# Revit family: Hager-Golf-IP40-Plain_Door-syst-NoHosted-PL-pl
name_source: partatom
category: Electrical Equipment
units: mm (PartAtom-declared; Revit-internal decimal feet)

## family parameters
Always vertical = Yes
Cut with Voids When Loaded = No
Panel Configuration = Two Columns, Circuits Across
Part Type = Panelboard
Room Calculation Point = No
Round Connector Dimension = Use Diameter
Shared = No
Work Plane-Based = Yes

## types (36) — shared parameters
Default Elevation = 1219 mm
EF000116 - Numer RAL = 9010
EF001062 - Wykonane zgodnie z Dyrektywą Kompatybilności Elektromagnetycznej EMC = No
EF004462 - Rodzaj zamknięcia = EV000154 - Inne
EF006244 - Transparentna pokrywa/drzwi = No
EF006306 - Z zamkiem = No
HG000001 - Liczba kolumn = 1
HG000002 - Z drzwiami lub pokrywą = Yes
HG000003 - Zakres = Golf
HG000005 - Grubość = 3 mm  [stored 0.00984252 ft]
HG000009 - Drzwi dwuskrzydłowe = No
HG000010 - Drzwi asymetryczne = No
HG000011 - Puste rzędy od dołu = No
HG000017 - Odległość między biegunami = 18 mm  [stored 0.0590551 ft]
Manufacturer = Hager
Type Comments = Golf
zero-valued in all types: HG000007 - Liczba pustych kolumn, HG000008 - Liczba pustych rzędów

## per-type parameters (varying)
| type | EF000003 - Sposób montażu | EF000007 - Kolor | EF000008 - Szerokość | EF000040 - Wysokość | EF000049 - Głębokość | EF000118 - Z płytą montażową | EF000218 - Głębokość wbudowania | EF000266 - Liczba rzędów | EF000332 - Wysokość wbudowania | EF000339 - Rodzaj pokrywy | EF000846 - Szerokość wbudowania | EF001088 - Możliwość rozbudowy | EF001131 - Głębokość wewnętrzna | EF001134 - Szyna DIN | EF001596 - Materiał obudowy | EF002950 - Szerokość wyrażona liczbą modułów | EF005474 - Stopień ochrony (IP) | EF009212 - Wykonanie pokrywy | EF015776 - Listwa zaciskowa uziemienia | EF015777 - Listwa zaciskowa przewodu neutralnego | EF015941 - Drzwi przepuszczające sygnał | HG000004 - Referencja producenta | HG000006 - Montaż podtynkowy | Model |
| Montaż natynkowy  S137.5 W183.5 G98.5 4 Jednostki dywizyjne - VS104PD | EV000384 - Montaż natynkowy |  | 138 mm  [stored 0.452756 ft] | 184 mm  [stored 0.603675 ft] | 98 mm  [stored 0.321522 ft] | No | 0 mm  [stored 0 ft] | 1 | 0 mm  [stored 0 ft] |  | 0 mm  [stored 0 ft] | No | 0 mm  [stored 0 ft] | No |  | 4 |  |  | No | No | No | VS104PD | No | VS104PD |
| Montaż natynkowy  S282 W252 G99 12 Jednostki dywizyjne - VS112PZB | EV000384 - Montaż natynkowy | EV000202 - Biały | 282 mm | 252 mm  [stored 0.826772 ft] | 99 mm  [stored 0.324803 ft] | No | 0 mm  [stored 0 ft] | 1 | 0 mm  [stored 0 ft] | EV004216 - Drzwi | 0 mm  [stored 0 ft] | Yes | 99 mm  [stored 0.324803 ft] | Yes | EV000139 - Tworzywo sztuczne | 12 |  | EV009916 - Z otworem | No | No | Yes | VS112PZB | No | VS112PZB |
| Montaż natynkowy  S282 W377 G99 12 Jednostki dywizyjne - VS212PZB | EV000384 - Montaż natynkowy | EV000202 - Biały | 282 mm | 377 mm  [stored 1.23688 ft] | 99 mm  [stored 0.324803 ft] | No | 0 mm  [stored 0 ft] | 2 | 0 mm  [stored 0 ft] | EV004216 - Drzwi | 0 mm  [stored 0 ft] | Yes | 99 mm  [stored 0.324803 ft] | Yes | EV000139 - Tworzywo sztuczne | 12 |  | EV009916 - Z otworem | No | No | Yes | VS212PZB | No | VS212PZB |
| Montaż natynkowy  S390 W377 G99 18 Jednostki dywizyjne - VS218PZE | EV000384 - Montaż natynkowy | EV000202 - Biały | 390 mm  [stored 1.27953 ft] | 377 mm  [stored 1.23688 ft] | 99 mm  [stored 0.324803 ft] | Yes | 0 mm  [stored 0 ft] | 2 | 0 mm  [stored 0 ft] | EV004216 - Drzwi | 0 mm  [stored 0 ft] | Yes | 99 mm  [stored 0.324803 ft] | Yes | EV000139 - Tworzywo sztuczne | 18 |  | EV009916 - Z otworem | No | No | Yes | VS218PZE | No | VS218PZE |
| Montaż natynkowy  S390 W377 G99 18 Jednostki dywizyjne - VS218PZF | EV000384 - Montaż natynkowy | EV000202 - Biały | 390 mm  [stored 1.27953 ft] | 377 mm  [stored 1.23688 ft] | 99 mm  [stored 0.324803 ft] | Yes | 0 mm  [stored 0 ft] | 2 | 0 mm  [stored 0 ft] | EV004216 - Drzwi | 0 mm  [stored 0 ft] | Yes | 99 mm  [stored 0.324803 ft] | Yes | EV000139 - Tworzywo sztuczne | 18 |  | EV009916 - Z otworem | No | No | Yes | VS218PZF | No | VS218PZF |
| Montaż natynkowy  S390 W500 G99 18 Jednostki dywizyjne - VS318PZF | EV000384 - Montaż natynkowy | EV000202 - Biały | 390 mm  [stored 1.27953 ft] | 500 mm  [stored 1.64042 ft] | 99 mm  [stored 0.324803 ft] | Yes | 0 mm  [stored 0 ft] | 3 | 0 mm  [stored 0 ft] | EV004216 - Drzwi | 0 mm  [stored 0 ft] | Yes | 99 mm  [stored 0.324803 ft] | Yes | EV000139 - Tworzywo sztuczne | 18 |  | EV009916 - Z otworem | No | No | Yes | VS318PZF | No | VS318PZF |
| Montaż natynkowy  S390 W647 G99 18 Jednostki dywizyjne - VS418PZF | EV000384 - Montaż natynkowy | EV000202 - Biały | 390 mm  [stored 1.27953 ft] | 647 mm  [stored 2.1227 ft] | 99 mm  [stored 0.324803 ft] | Yes | 0 mm  [stored 0 ft] | 4 | 0 mm  [stored 0 ft] | EV004216 - Drzwi | 0 mm  [stored 0 ft] | Yes | 99 mm  [stored 0.324803 ft] | Yes | EV000139 - Tworzywo sztuczne | 18 |  | EV009916 - Z otworem | No | No | Yes | VS418PZF | No | VS418PZF |
| Montaż natynkowy IP40 S209.5 W183.5 G98.5 8 Jednostki dywizyjne - VS108PD | EV000384 - Montaż natynkowy |  | 210 mm  [stored 0.688976 ft] | 184 mm  [stored 0.603675 ft] | 98 mm  [stored 0.321522 ft] | No | 0 mm  [stored 0 ft] | 1 | 0 mm  [stored 0 ft] |  | 0 mm  [stored 0 ft] | No | 0 mm  [stored 0 ft] | No |  | 8 | EV006415 - IP40 |  | No | No | No | VS108PD | No | VS108PD |
| Montaż natynkowy IP40 S281.5 W251.5 G98.5 12 Jednostki dywizyjne - VS112PD | EV000384 - Montaż natynkowy |  | 282 mm | 252 mm  [stored 0.826772 ft] | 98 mm  [stored 0.321522 ft] | No | 0 mm  [stored 0 ft] | 1 | 0 mm  [stored 0 ft] |  | 0 mm  [stored 0 ft] | No | 0 mm  [stored 0 ft] | No |  | 12 | EV006415 - IP40 |  | No | No | No | VS112PD | No | VS112PD |
| Montaż natynkowy IP40 S282 W377 G99 12 Jednostki dywizyjne - VS212PD | EV000384 - Montaż natynkowy | EV000202 - Biały | 282 mm | 377 mm  [stored 1.23688 ft] | 99 mm  [stored 0.324803 ft] | No | 0 mm  [stored 0 ft] | 2 | 0 mm  [stored 0 ft] | EV004216 - Drzwi | 0 mm  [stored 0 ft] | Yes | 99 mm  [stored 0.324803 ft] | Yes | EV000139 - Tworzywo sztuczne | 12 | EV006415 - IP40 | EV000116 - Zamknięty | Yes | Yes | Yes | VS212PD | No | VS212PD |
| Montaż natynkowy IP40 S282 W500 G99 12 Jednostki dywizyjne - VS312PD | EV000384 - Montaż natynkowy | EV000202 - Biały | 282 mm | 500 mm  [stored 1.64042 ft] | 99 mm  [stored 0.324803 ft] | No | 0 mm  [stored 0 ft] | 3 | 0 mm  [stored 0 ft] | EV004216 - Drzwi | 0 mm  [stored 0 ft] | Yes | 99 mm  [stored 0.324803 ft] | Yes | EV000139 - Tworzywo sztuczne | 12 | EV006415 - IP40 | EV000116 - Zamknięty | Yes | Yes | Yes | VS312PD | No | VS312PD |
| Montaż natynkowy IP40 S282 W647 G99 12 Jednostki dywizyjne - VS412PD | EV000384 - Montaż natynkowy | EV000202 - Biały | 282 mm | 647 mm  [stored 2.1227 ft] | 99 mm  [stored 0.324803 ft] | No | 0 mm  [stored 0 ft] | 4 | 0 mm  [stored 0 ft] | EV004216 - Drzwi | 0 mm  [stored 0 ft] | Yes | 99 mm  [stored 0.324803 ft] | Yes | EV000139 - Tworzywo sztuczne | 12 | EV006415 - IP40 | EV000116 - Zamknięty | Yes | Yes | Yes | VS412PD | No | VS412PD |
| Montaż natynkowy IP40 S390 W252 G99 18 Jednostki dywizyjne - VS118PD | EV000384 - Montaż natynkowy | EV000202 - Biały | 390 mm  [stored 1.27953 ft] | 252 mm  [stored 0.826772 ft] | 99 mm  [stored 0.324803 ft] | No | 0 mm  [stored 0 ft] | 1 | 0 mm  [stored 0 ft] | EV004216 - Drzwi | 0 mm  [stored 0 ft] | Yes | 99 mm  [stored 0.324803 ft] | Yes | EV000139 - Tworzywo sztuczne | 18 | EV006415 - IP40 | EV000116 - Zamknięty | Yes | Yes | Yes | VS118PD | No | VS118PD |
| Montaż natynkowy IP40 S390 W377 G99 18 Jednostki dywizyjne - VS218PD | EV000384 - Montaż natynkowy | EV000202 - Biały | 390 mm  [stored 1.27953 ft] | 377 mm  [stored 1.23688 ft] | 99 mm  [stored 0.324803 ft] | No | 0 mm  [stored 0 ft] | 2 | 0 mm  [stored 0 ft] | EV004216 - Drzwi | 0 mm  [stored 0 ft] | Yes | 99 mm  [stored 0.324803 ft] | Yes | EV000139 - Tworzywo sztuczne | 18 | EV006415 - IP40 | EV000116 - Zamknięty | Yes | Yes | Yes | VS218PD | No | VS218PD |
| Montaż natynkowy IP40 S390 W377 G99 18 Jednostki dywizyjne - VS218PDE | EV000384 - Montaż natynkowy | EV000202 - Biały | 390 mm  [stored 1.27953 ft] | 377 mm  [stored 1.23688 ft] | 99 mm  [stored 0.324803 ft] | No | 0 mm  [stored 0 ft] | 2 | 0 mm  [stored 0 ft] | EV004216 - Drzwi | 0 mm  [stored 0 ft] | Yes | 99 mm  [stored 0.324803 ft] | Yes | EV000139 - Tworzywo sztuczne | 18 | EV006415 - IP40 | EV000116 - Zamknięty | Yes | Yes | Yes | VS218PDE | No | VS218PDE |
| Montaż natynkowy IP40 S390 W500 G99 18 Jednostki dywizyjne - VS318PD | EV000384 - Montaż natynkowy | EV000202 - Biały | 390 mm  [stored 1.27953 ft] | 500 mm  [stored 1.64042 ft] | 99 mm  [stored 0.324803 ft] | No | 0 mm  [stored 0 ft] | 3 | 0 mm  [stored 0 ft] | EV004216 - Drzwi | 0 mm  [stored 0 ft] | Yes | 99 mm  [stored 0.324803 ft] | Yes | EV000139 - Tworzywo sztuczne | 18 | EV006415 - IP40 | EV000116 - Zamknięty | Yes | Yes | Yes | VS318PD | No | VS318PD |
| Montaż natynkowy IP40 S390 W647 G99 18 Jednostki dywizyjne - VS418PD | EV000384 - Montaż natynkowy | EV000202 - Biały | 390 mm  [stored 1.27953 ft] | 647 mm  [stored 2.1227 ft] | 99 mm  [stored 0.324803 ft] | No | 0 mm  [stored 0 ft] | 4 | 0 mm  [stored 0 ft] | EV004216 - Drzwi | 0 mm  [stored 0 ft] | Yes | 99 mm  [stored 0.324803 ft] | Yes | EV000139 - Tworzywo sztuczne | 18 | EV006415 - IP40 | EV000116 - Zamknięty | Yes | Yes | Yes | VS418PD | No | VS418PD |
| Montaż natynkowy IP40 S462 W252 G99 22 Jednostki dywizyjne - VS122PD | EV000384 - Montaż natynkowy | EV000202 - Biały | 462 mm  [stored 1.51575 ft] | 252 mm  [stored 0.826772 ft] | 99 mm  [stored 0.324803 ft] | No | 0 mm  [stored 0 ft] | 1 | 0 mm  [stored 0 ft] | EV004216 - Drzwi | 0 mm  [stored 0 ft] | Yes | 99 mm  [stored 0.324803 ft] | Yes | EV000139 - Tworzywo sztuczne | 22 | EV006415 - IP40 | EV000116 - Zamknięty | Yes | Yes | Yes | VS122PD | No | VS122PD |
| Montaż podtynkowy  S204 W225 G97.5 4 Jednostki dywizyjne - VF104PD | EV000383 - Montaż podtynkowy |  | 204 mm | 225 mm  [stored 0.738189 ft] | 98 mm  [stored 0.321522 ft] | No | 72 mm  [stored 0.23622 ft] | 1 | 189 mm  [stored 0.620079 ft] |  | 170 mm  [stored 0.557743 ft] | No | 0 mm  [stored 0 ft] | No | EV000139 - Tworzywo sztuczne | 4 |  |  | No | No | No | VF104PD | Yes | VF104PD |
| Montaż podtynkowy  S275 W225 G97.5 8 Jednostki dywizyjne - VF108PD | EV000383 - Montaż podtynkowy |  | 275 mm | 225 mm  [stored 0.738189 ft] | 98 mm  [stored 0.321522 ft] | No | 72 mm  [stored 0.23622 ft] | 1 | 189 mm  [stored 0.620079 ft] |  | 242 mm  [stored 0.793963 ft] | No | 0 mm  [stored 0 ft] | No | EV000139 - Tworzywo sztuczne | 8 |  |  | No | No | No | VF108PD | Yes | VF108PD |
| Montaż podtynkowy  S352 W293 G97.5 12 Jednostki dywizyjne - VF112PZB | EV000383 - Montaż podtynkowy | EV000202 - Biały | 352 mm  [stored 1.15486 ft] | 293 mm | 98 mm  [stored 0.321522 ft] | No | 72 mm  [stored 0.23622 ft] | 1 | 250 mm  [stored 0.82021 ft] | EV004216 - Drzwi | 318 mm  [stored 1.04331 ft] | Yes | 98 mm  [stored 0.321522 ft] | Yes | EV000139 - Tworzywo sztuczne | 12 |  | EV009916 - Z otworem | No | No | Yes | VF112PZB | Yes | VF112PZB |
| Montaż podtynkowy  S352 W543 G97.5 12 Jednostki dywizyjne - VF312PZB | EV000383 - Montaż podtynkowy | EV000202 - Biały | 352 mm  [stored 1.15486 ft] | 543 mm  [stored 1.7815 ft] | 98 mm  [stored 0.321522 ft] | No | 72 mm  [stored 0.23622 ft] | 3 | 495 mm  [stored 1.62402 ft] | EV004216 - Drzwi | 318 mm  [stored 1.04331 ft] | Yes | 98 mm  [stored 0.321522 ft] | Yes | EV000139 - Tworzywo sztuczne | 12 |  | EV009916 - Z otworem | No | No | Yes | VF312PZB | Yes | VF312PZB |
| Montaż podtynkowy  S382 W418 G97.5 12 Jednostki dywizyjne - VF212PZB | EV000383 - Montaż podtynkowy | EV000202 - Biały | 382 mm  [stored 1.25328 ft] | 418 mm  [stored 1.37139 ft] | 98 mm  [stored 0.321522 ft] | No | 72 mm  [stored 0.23622 ft] | 2 | 370 mm  [stored 1.21391 ft] | EV004216 - Drzwi | 318 mm  [stored 1.04331 ft] | Yes | 98 mm  [stored 0.321522 ft] | Yes | EV000139 - Tworzywo sztuczne | 12 |  | EV009916 - Z otworem | No | No | Yes | VF212PZB | Yes | VF212PZB |
| Montaż podtynkowy  S460 W418 G97.5 18 Jednostki dywizyjne - VF218PZB | EV000383 - Montaż podtynkowy | EV000202 - Biały | 460 mm  [stored 1.50919 ft] | 418 mm  [stored 1.37139 ft] | 98 mm  [stored 0.321522 ft] | No | 72 mm  [stored 0.23622 ft] | 2 | 375 mm  [stored 1.23031 ft] | EV004216 - Drzwi | 426 mm  [stored 1.39764 ft] | Yes | 98 mm  [stored 0.321522 ft] | Yes | EV000139 - Tworzywo sztuczne | 18 |  | EV009916 - Z otworem | No | No | Yes | VF218PZB | Yes | VF218PZB |
| Montaż podtynkowy  S460 W418 G97.5 18 Jednostki dywizyjne - VF218PZF | EV000383 - Montaż podtynkowy | EV000202 - Biały | 460 mm  [stored 1.50919 ft] | 418 mm  [stored 1.37139 ft] | 98 mm  [stored 0.321522 ft] | Yes | 72 mm  [stored 0.23622 ft] | 2 | 375 mm  [stored 1.23031 ft] | EV004216 - Drzwi | 426 mm  [stored 1.39764 ft] | Yes | 98 mm  [stored 0.321522 ft] | Yes | EV000139 - Tworzywo sztuczne | 18 |  | EV009916 - Z otworem | No | No | Yes | VF218PZF | Yes | VF218PZF |
| Montaż podtynkowy  S460 W543 G97.5 18 Jednostki dywizyjne - VF318PZF | EV000383 - Montaż podtynkowy | EV000202 - Biały | 460 mm  [stored 1.50919 ft] | 543 mm  [stored 1.7815 ft] | 98 mm  [stored 0.321522 ft] | Yes | 72 mm  [stored 0.23622 ft] | 3 | 495 mm  [stored 1.62402 ft] | EV004216 - Drzwi | 426 mm  [stored 1.39764 ft] | Yes | 98 mm  [stored 0.321522 ft] | Yes | EV000139 - Tworzywo sztuczne | 18 |  | EV009916 - Z otworem | No | No | Yes | VF318PZF | Yes | VF318PZF |
| Montaż podtynkowy  S460 W688 G97.5 18 Jednostki dywizyjne - VF418PZF | EV000383 - Montaż podtynkowy | EV000202 - Biały | 460 mm  [stored 1.50919 ft] | 688 mm | 98 mm  [stored 0.321522 ft] | Yes | 72 mm  [stored 0.23622 ft] | 4 | 640 mm  [stored 2.09974 ft] | EV004216 - Drzwi | 426 mm  [stored 1.39764 ft] | Yes | 98 mm  [stored 0.321522 ft] | Yes | EV000139 - Tworzywo sztuczne | 18 |  | EV009916 - Z otworem | No | No | Yes | VF418PZF | Yes | VF418PZF |
| Montaż podtynkowy IP40 S352 W293 G97.5 12 Jednostki dywizyjne - VF112PD | EV000383 - Montaż podtynkowy |  | 352 mm  [stored 1.15486 ft] | 293 mm | 98 mm  [stored 0.321522 ft] | No | 72 mm  [stored 0.23622 ft] | 1 | 257 mm  [stored 0.843176 ft] |  | 318 mm  [stored 1.04331 ft] | No | 0 mm  [stored 0 ft] | No | EV000139 - Tworzywo sztuczne | 12 | EV006415 - IP40 |  | No | No | No | VF112PD | Yes | VF112PD |
| Montaż podtynkowy IP40 S352 W543 G97.5 12 Jednostki dywizyjne - VF312PD | EV000383 - Montaż podtynkowy | EV000202 - Biały | 352 mm  [stored 1.15486 ft] | 543 mm  [stored 1.7815 ft] | 98 mm  [stored 0.321522 ft] | No | 72 mm  [stored 0.23622 ft] | 3 | 507 mm  [stored 1.66339 ft] | EV004216 - Drzwi | 318 mm  [stored 1.04331 ft] | Yes | 98 mm  [stored 0.321522 ft] | Yes | EV000139 - Tworzywo sztuczne | 12 | EV006415 - IP40 | EV000116 - Zamknięty | Yes | Yes | Yes | VF312PD | Yes | VF312PD |
| Montaż podtynkowy IP40 S352 W688 G97.5 12 Jednostki dywizyjne - VF412PD | EV000383 - Montaż podtynkowy | EV000202 - Biały | 352 mm  [stored 1.15486 ft] | 688 mm | 98 mm  [stored 0.321522 ft] | No | 72 mm  [stored 0.23622 ft] | 4 | 652 mm  [stored 2.13911 ft] | EV004216 - Drzwi | 318 mm  [stored 1.04331 ft] | Yes | 98 mm  [stored 0.321522 ft] | Yes | EV000139 - Tworzywo sztuczne | 12 | EV006415 - IP40 | EV000116 - Zamknięty | Yes | Yes | Yes | VF412PD | Yes | VF412PD |
| Montaż podtynkowy IP40 S382 W418 G97.5 12 Jednostki dywizyjne - VF212PD | EV000383 - Montaż podtynkowy | EV000202 - Biały | 382 mm  [stored 1.25328 ft] | 418 mm  [stored 1.37139 ft] | 98 mm  [stored 0.321522 ft] | No | 72 mm  [stored 0.23622 ft] | 2 | 382 mm  [stored 1.25328 ft] | EV004216 - Drzwi | 318 mm  [stored 1.04331 ft] | Yes | 98 mm  [stored 0.321522 ft] | Yes | EV000139 - Tworzywo sztuczne | 12 | EV006415 - IP40 | EV000116 - Zamknięty | Yes | Yes | Yes | VF212PD | Yes | VF212PD |
| Montaż podtynkowy IP40 S460 W293 G97.5 18 Jednostki dywizyjne - VF118PD | EV000383 - Montaż podtynkowy | EV000202 - Biały | 460 mm  [stored 1.50919 ft] | 293 mm | 98 mm  [stored 0.321522 ft] | No | 72 mm  [stored 0.23622 ft] | 1 | 257 mm  [stored 0.843176 ft] | EV004216 - Drzwi | 426 mm  [stored 1.39764 ft] | Yes | 98 mm  [stored 0.321522 ft] | Yes | EV000139 - Tworzywo sztuczne | 18 | EV006415 - IP40 | EV000116 - Zamknięty | Yes | Yes | Yes | VF118PD | Yes | VF118PD |
| Montaż podtynkowy IP40 S460 W418 G97.5 18 Jednostki dywizyjne - VF218PD | EV000383 - Montaż podtynkowy | EV000202 - Biały | 460 mm  [stored 1.50919 ft] | 418 mm  [stored 1.37139 ft] | 98 mm  [stored 0.321522 ft] | No | 72 mm  [stored 0.23622 ft] | 2 | 382 mm  [stored 1.25328 ft] | EV004216 - Drzwi | 426 mm  [stored 1.39764 ft] | Yes | 98 mm  [stored 0.321522 ft] | Yes | EV000139 - Tworzywo sztuczne | 18 | EV006415 - IP40 | EV000116 - Zamknięty | Yes | Yes | Yes | VF218PD | Yes | VF218PD |
| Montaż podtynkowy IP40 S460 W543 G97.5 18 Jednostki dywizyjne - VF318PD | EV000383 - Montaż podtynkowy | EV000202 - Biały | 460 mm  [stored 1.50919 ft] | 543 mm  [stored 1.7815 ft] | 98 mm  [stored 0.321522 ft] | No | 72 mm  [stored 0.23622 ft] | 3 | 507 mm  [stored 1.66339 ft] | EV004216 - Drzwi | 426 mm  [stored 1.39764 ft] | Yes | 98 mm  [stored 0.321522 ft] | Yes | EV000139 - Tworzywo sztuczne | 18 | EV006415 - IP40 | EV000116 - Zamknięty | Yes | Yes | Yes | VF318PD | Yes | VF318PD |
| Montaż podtynkowy IP40 S460 W688 G97.5 18 Jednostki dywizyjne - VF418PD | EV000383 - Montaż podtynkowy | EV000202 - Biały | 460 mm  [stored 1.50919 ft] | 688 mm | 98 mm  [stored 0.321522 ft] | No | 72 mm  [stored 0.23622 ft] | 4 | 652 mm  [stored 2.13911 ft] | EV004216 - Drzwi | 426 mm  [stored 1.39764 ft] | Yes | 98 mm  [stored 0.321522 ft] | Yes | EV000139 - Tworzywo sztuczne | 18 | EV006415 - IP40 | EV000116 - Zamknięty | Yes | Yes | Yes | VF418PD | Yes | VF418PD |
| Montaż podtynkowy IP40 S532 W293 G97.5 22 Jednostki dywizyjne - VF122PD | EV000383 - Montaż podtynkowy | EV000202 - Biały | 532 mm  [stored 1.74541 ft] | 293 mm | 98 mm  [stored 0.321522 ft] | No | 72 mm  [stored 0.23622 ft] | 1 | 257 mm  [stored 0.843176 ft] | EV004216 - Drzwi | 498 mm  [stored 1.63386 ft] | Yes | 98 mm  [stored 0.321522 ft] | Yes | EV000139 - Tworzywo sztuczne | 22 | EV006415 - IP40 | EV000116 - Zamknięty | Yes | Yes | Yes | VF122PD | Yes | VF122PD |

note: [stored X ft] marks values corroborated as IEEE doubles in the binary element streams (Revit-internal decimal feet)

## geometry (parser evidence)
native form markers: Sweep x13
no freeform markers — native parametric forms only
